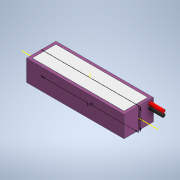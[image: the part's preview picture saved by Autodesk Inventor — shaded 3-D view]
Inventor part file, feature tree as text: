
AUTODESK INVENTOR PART (.ipt)
format: ipt  version: 2021 (Build 250183000, 183)  size: 136,704 bytes
history: native  units: mm
features: sketch x3, extrude x3
ambient origin geometry x8: Origin, YZ Plane, XZ Plane, XY Plane, X Axis, Y Axis, Z Axis, Center Point
bodies: Volumenkörper1 (feature_tree)
feature tree (6):
  sketch  "Skizze1"  dims[d0=143.0mm d1=31.0mm]
  extrude  "Extrusion1"  Depth=31.0mm
  extrude  "Extrusion2"  Depth=4.0mm
  extrude  "Extrusion3"  Depth=4.0mm
  sketch  "Skizze2"  dims[d2=43.0mm d3=0.0mm d5=4.0mm]
  sketch  "Skizze3"  dims[d6=4.0mm d7=4.0mm d8=4.0mm d9=0.2mm d10=0.0mm d11=5.0mm d12=5.0mm d13=5.0mm d14=5.0mm d15=5.0mm d16=5.5mm d17=20.0mm d18=0.0mm]
